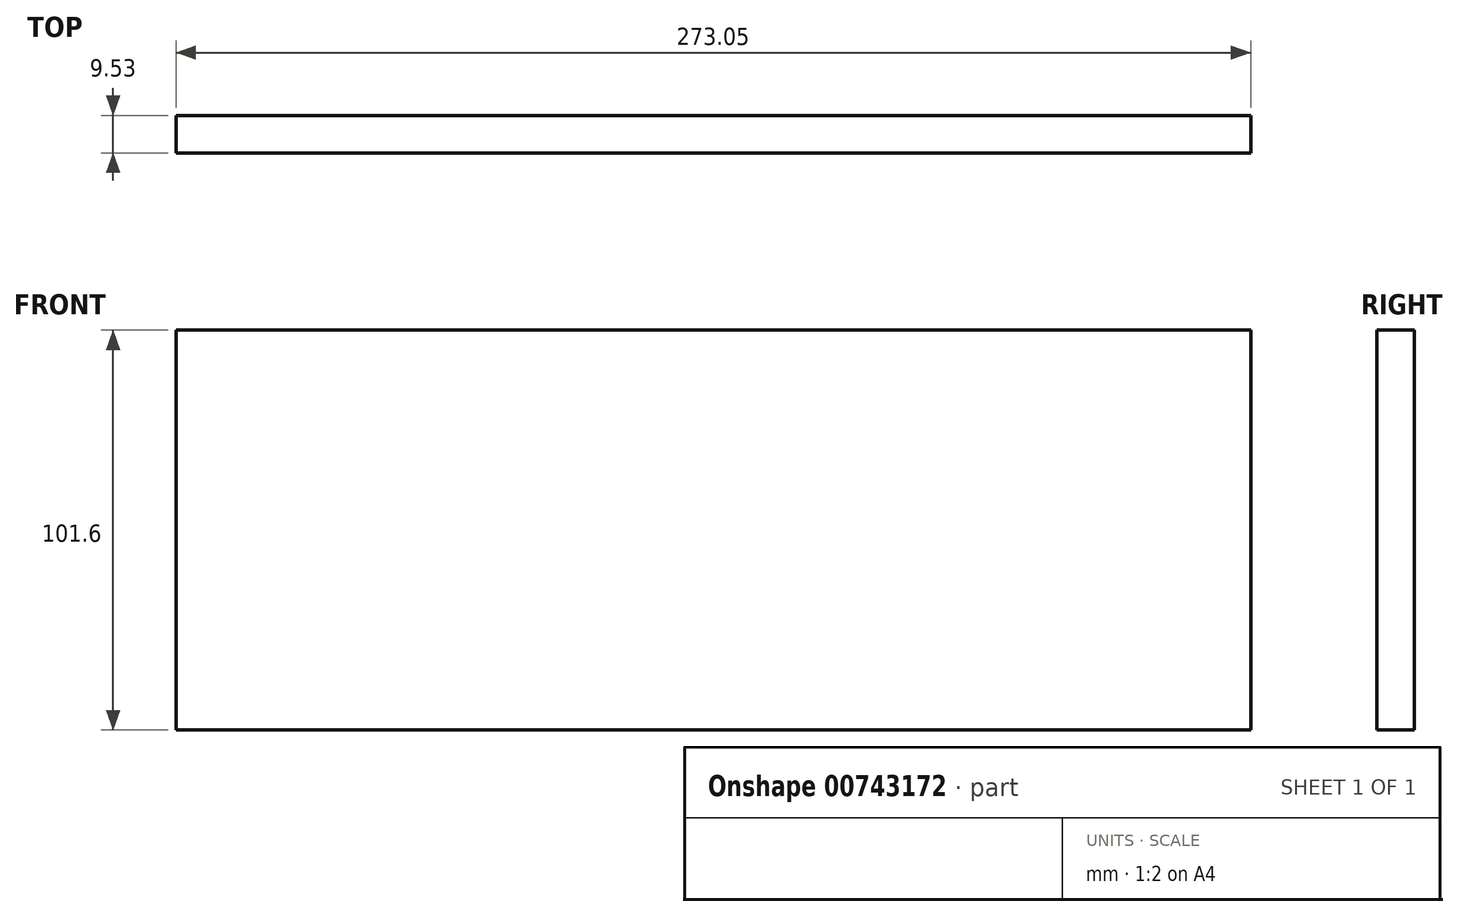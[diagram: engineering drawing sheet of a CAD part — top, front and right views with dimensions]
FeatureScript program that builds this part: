
annotation { "Feature Type Name" : "Feature", "Feature Type Description" : "" }
export const myFeature = defineFeature(function(context is Context, id is Id, definition is map)
    precondition{}
    {
        {
            var Q0;
            Q0=qCreatedBy(makeId("Front.planeOp"),FACE);
            var sketch = newSketch(context, id + "F0", { "sketchPlane" : qUnion([Q0])});
            skLineSegment(sketch, "E0.bottom", {"start": v(0, 0) * mm, "end": v(273.05, 0) * mm});
            skLineSegment(sketch, "E0.top", {"start": v(0, 101.6) * mm, "end": v(273.05, 101.6) * mm});
            skLineSegment(sketch, "E0.left", {"start": v(0, 0) * mm, "end": v(0, 101.6) * mm});
            skLineSegment(sketch, "E0.right", {"start": v(273.05, 0) * mm, "end": v(273.05, 101.6) * mm});
            skSolve(sketch);
        }
        {
            var Q0;
            Q0=makeQuery(id+"F0.imprint","IMPRINT",FACE,{"disambiguationData":[TD([[makeQuery(id+"F0.imprint","IMPRINT",EDGE,{"derivedFrom":sQuery(id+"F0.wireOp",EDGE,"E0.bottom")}),1.0]])]});
            extrude(context, id + "F1", {"entities" : qUnion([Q0]), "depth" : 9.52 * mm, "offsetDistance" : 25.4 * mm});
        }
    });
